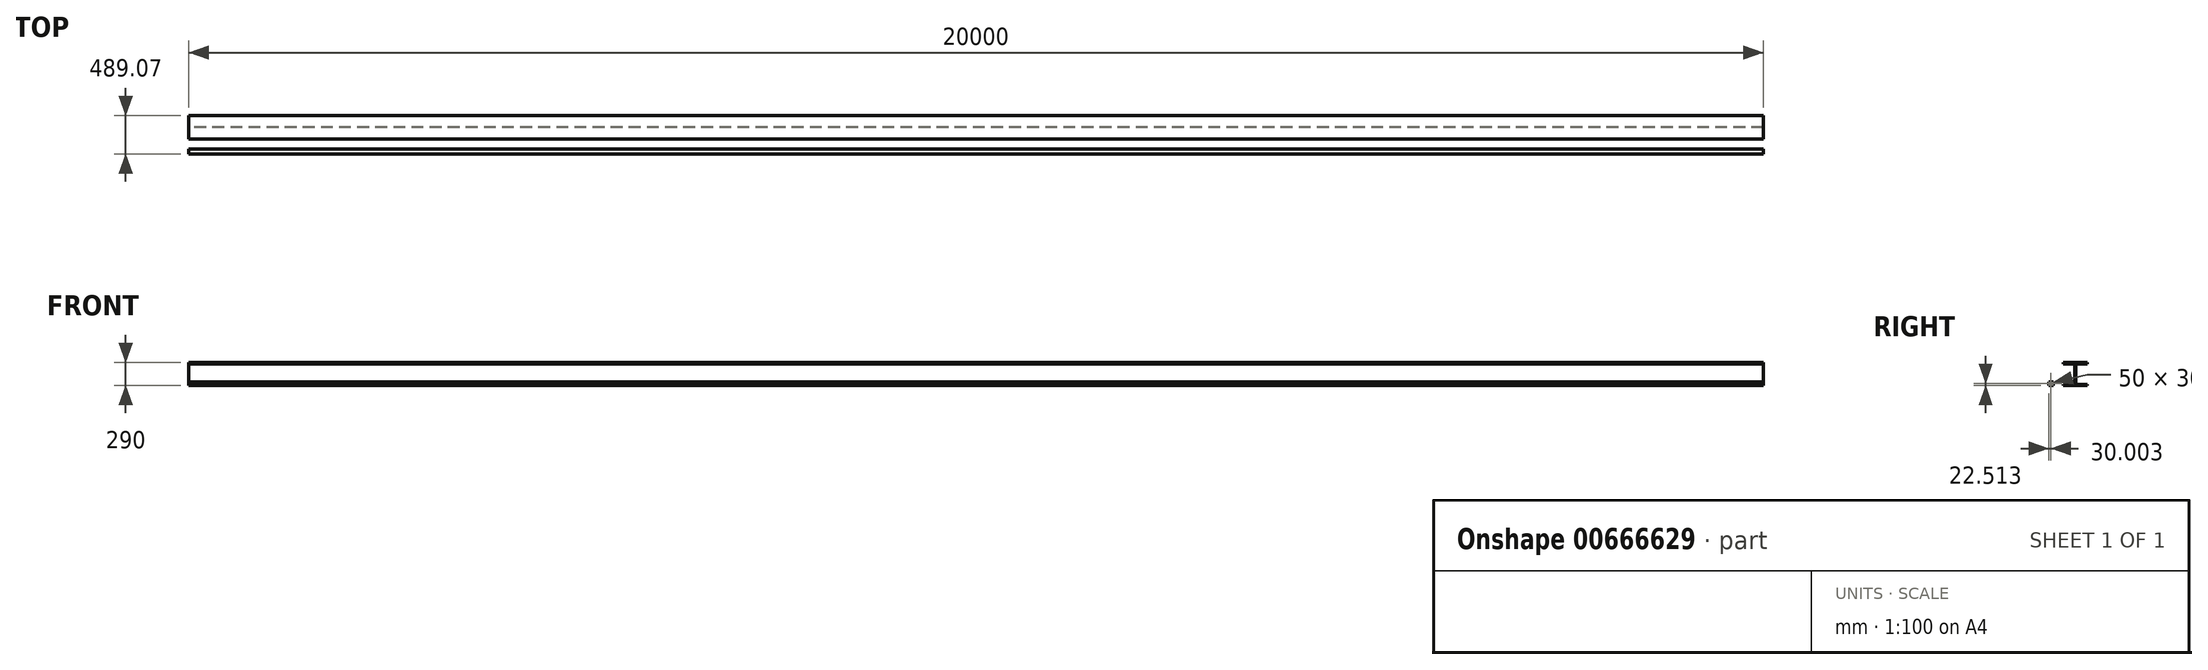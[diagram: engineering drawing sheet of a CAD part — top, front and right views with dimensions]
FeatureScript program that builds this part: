
annotation { "Feature Type Name" : "Feature", "Feature Type Description" : "" }
export const myFeature = defineFeature(function(context is Context, id is Id, definition is map)
    precondition{}
    {
        {
            var Q0;
            Q0=qCreatedBy(makeId("Right.planeOp"),FACE);
            var sketch = newSketch(context, id + "F0", { "sketchPlane" : qUnion([Q0])});
            skLineSegment(sketch, "E0", {"start": v(-31.84, -28.94) * mm, "end": v(268.16, -28.94) * mm});
            skLineSegment(sketch, "E1", {"start": v(268.16, -28.94) * mm, "end": v(268.16, -13.94) * mm});
            skLineSegment(sketch, "E2", {"start": v(268.16, -13.94) * mm, "end": v(123.16, -13.94) * mm});
            skLineSegment(sketch, "E3", {"start": v(123.16, -13.94) * mm, "end": v(123.16, 246.06) * mm});
            skLineSegment(sketch, "E4", {"start": v(123.16, 246.06) * mm, "end": v(268.16, 246.06) * mm});
            skLineSegment(sketch, "E5", {"start": v(268.16, 246.06) * mm, "end": v(268.16, 261.06) * mm});
            skLineSegment(sketch, "E6", {"start": v(268.16, 261.06) * mm, "end": v(-31.84, 261.06) * mm});
            skLineSegment(sketch, "E7", {"start": v(-31.84, 261.06) * mm, "end": v(-31.84, 246.06) * mm});
            skLineSegment(sketch, "E8", {"start": v(-31.84, 246.06) * mm, "end": v(113.16, 246.06) * mm});
            skLineSegment(sketch, "E9", {"start": v(113.16, 246.06) * mm, "end": v(113.16, -13.94) * mm});
            skLineSegment(sketch, "E10", {"start": v(113.16, -13.94) * mm, "end": v(-31.84, -13.94) * mm});
            skLineSegment(sketch, "E11", {"start": v(-31.84, -13.94) * mm, "end": v(-31.84, -28.94) * mm});
            skSolve(sketch);
        }
        {
            var Q0;
            Q0=makeQuery(id+"F0.imprint","IMPRINT",FACE,{"disambiguationData":[TD([[makeQuery(id+"F0.imprint","IMPRINT",EDGE,{"derivedFrom":sQuery(id+"F0.wireOp",EDGE,"E0")}),1.0]])]});
            extrude(context, id + "F1", {"entities" : qUnion([Q0]), "depth" : 20000 * mm, "offsetDistance" : 25 * mm});
        }
        {
            var Q0;
            Q0=qCreatedBy(makeId("Right.planeOp"),FACE);
            var sketch = newSketch(context, id + "F2", { "sketchPlane" : qUnion([Q0])});
            skLineSegment(sketch, "E12.bottom", {"start": v(-160.9, -26.43) * mm, "end": v(-220.9, -26.43) * mm});
            skLineSegment(sketch, "E12.top", {"start": v(-160.9, 13.57) * mm, "end": v(-220.9, 13.57) * mm});
            skLineSegment(sketch, "E12.left", {"start": v(-160.9, -26.43) * mm, "end": v(-160.9, 13.57) * mm});
            skLineSegment(sketch, "E12.right", {"start": v(-220.9, -26.43) * mm, "end": v(-220.9, 13.57) * mm});
            skPoint(sketch, "E12.middle", {"position": v(-190.9, -6.43) * mm});
            skLineSegment(sketch, "E13.bottom", {"start": v(-165.9, -21.43) * mm, "end": v(-215.9, -21.43) * mm});
            skLineSegment(sketch, "E13.top", {"start": v(-165.9, 8.57) * mm, "end": v(-215.9, 8.57) * mm});
            skLineSegment(sketch, "E13.left", {"start": v(-165.9, -21.43) * mm, "end": v(-165.9, 8.57) * mm});
            skLineSegment(sketch, "E13.right", {"start": v(-215.9, -21.43) * mm, "end": v(-215.9, 8.57) * mm});
            skSolve(sketch);
        }
        {
            var Q0;
            Q0=makeQuery(id+"F2.imprint","IMPRINT",FACE,{"disambiguationData":[TD([[makeQuery(id+"F2.imprint","IMPRINT",EDGE,{"derivedFrom":sQuery(id+"F2.wireOp",EDGE,"E12.bottom")}),-1.0]])]});
            extrude(context, id + "F3", {"entities" : qUnion([Q0]), "depth" : 20000 * mm, "offsetDistance" : 25 * mm});
        }
    });
